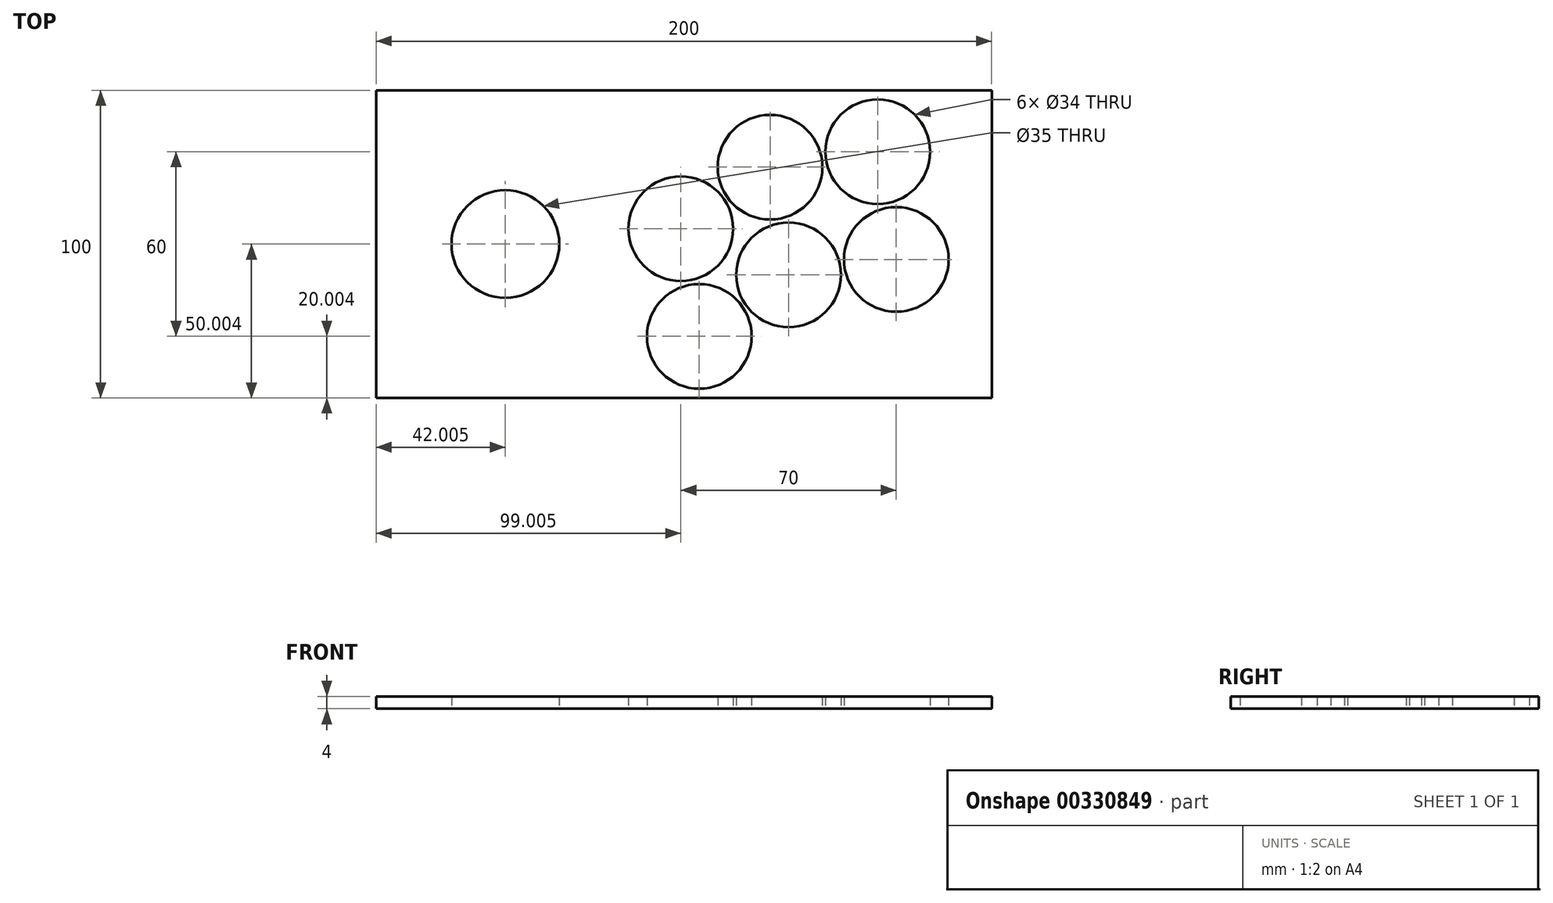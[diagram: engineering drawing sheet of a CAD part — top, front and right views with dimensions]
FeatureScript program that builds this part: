
annotation { "Feature Type Name" : "Feature", "Feature Type Description" : "" }
export const myFeature = defineFeature(function(context is Context, id is Id, definition is map)
    precondition{}
    {
        {
            var Q0;
            Q0=qCreatedBy(makeId("Top.planeOp"),FACE);
            var sketch = newSketch(context, id + "F0", { "sketchPlane" : qUnion([Q0])});
            skLineSegment(sketch, "E0.bottom", {"start": v(-132.17, 62.31) * mm, "end": v(67.83, 62.31) * mm});
            skLineSegment(sketch, "E0.top", {"start": v(-132.17, -37.69) * mm, "end": v(67.83, -37.69) * mm});
            skLineSegment(sketch, "E0.left", {"start": v(-132.17, 62.31) * mm, "end": v(-132.17, -37.69) * mm});
            skLineSegment(sketch, "E0.right", {"start": v(67.83, 62.31) * mm, "end": v(67.83, -37.69) * mm});
            skSolve(sketch);
        }
        {
            var Q0;
            Q0=makeQuery(id+"F0.imprint","IMPRINT",FACE,{"disambiguationData":[TD([[makeQuery(id+"F0.imprint","IMPRINT",EDGE,{"derivedFrom":sQuery(id+"F0.wireOp",EDGE,"E0.bottom")}),-1.0]])]});
            var sketch = newSketch(context, id + "F1", { "sketchPlane" : qUnion([Q0])});
            skCircle(sketch, "E1", {"center": v(-90.17, 12.31) * mm, "radius": 17.5 * mm});
            skCircle(sketch, "E2", {"center": v(-33.17, 17.31) * mm, "radius": 17 * mm});
            skCircle(sketch, "E3", {"center": v(-4.17, 37.31) * mm, "radius": 17 * mm});
            skCircle(sketch, "E4", {"center": v(30.83, 42.31) * mm, "radius": 17 * mm});
            skCircle(sketch, "E5", {"center": v(-27.17, -17.69) * mm, "radius": 17 * mm});
            skCircle(sketch, "E6", {"center": v(1.83, 2.31) * mm, "radius": 17 * mm});
            skCircle(sketch, "E7", {"center": v(36.83, 7.31) * mm, "radius": 17 * mm});
            skSolve(sketch);
        }
        {
            var Q0;
            Q0=makeQuery(id+"F0.imprint","IMPRINT",FACE,{"disambiguationData":[TD([[makeQuery(id+"F0.imprint","IMPRINT",EDGE,{"derivedFrom":sQuery(id+"F0.wireOp",EDGE,"E0.bottom")}),-1.0]])]});
            extrude(context, id + "F2", {"entities" : qUnion([Q0]), "depth" : 4 * mm});
        }
        {
            var Q0;
            Q0=makeQuery(id+"F1.imprint","IMPRINT",FACE,{"disambiguationData":[TD([[makeQuery(id+"F1.imprint","IMPRINT",EDGE,{"derivedFrom":sQuery(id+"F1.wireOp",EDGE,"E1")}),1.0]])]});
            var Q1;
            Q1=makeQuery(id+"F1.imprint","IMPRINT",FACE,{"disambiguationData":[TD([[makeQuery(id+"F1.imprint","IMPRINT",EDGE,{"derivedFrom":sQuery(id+"F1.wireOp",EDGE,"E5")}),1.0]])]});
            var Q2;
            Q2=makeQuery(id+"F1.imprint","IMPRINT",FACE,{"disambiguationData":[TD([[makeQuery(id+"F1.imprint","IMPRINT",EDGE,{"derivedFrom":sQuery(id+"F1.wireOp",EDGE,"E2")}),1.0]])]});
            var Q3;
            Q3=makeQuery(id+"F1.imprint","IMPRINT",FACE,{"disambiguationData":[TD([[makeQuery(id+"F1.imprint","IMPRINT",EDGE,{"derivedFrom":sQuery(id+"F1.wireOp",EDGE,"E6")}),1.0]])]});
            var Q4;
            Q4=makeQuery(id+"F1.imprint","IMPRINT",FACE,{"disambiguationData":[TD([[makeQuery(id+"F1.imprint","IMPRINT",EDGE,{"derivedFrom":sQuery(id+"F1.wireOp",EDGE,"E3")}),1.0]])]});
            var Q5;
            Q5=makeQuery(id+"F1.imprint","IMPRINT",FACE,{"disambiguationData":[TD([[makeQuery(id+"F1.imprint","IMPRINT",EDGE,{"derivedFrom":sQuery(id+"F1.wireOp",EDGE,"E7")}),1.0]])]});
            var Q6;
            Q6=makeQuery(id+"F1.imprint","IMPRINT",FACE,{"disambiguationData":[TD([[makeQuery(id+"F1.imprint","IMPRINT",EDGE,{"derivedFrom":sQuery(id+"F1.wireOp",EDGE,"E4")}),1.0]])]});
            extrude(context, id + "F3", {"entities" : qUnion([Q0, Q1, Q2, Q3, Q4, Q5, Q6]), "operationType" : NewBodyOperationType.REMOVE, "depth" : 4 * mm});
        }
    });
